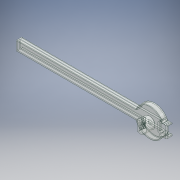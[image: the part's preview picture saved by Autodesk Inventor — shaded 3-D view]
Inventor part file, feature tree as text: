
AUTODESK INVENTOR PART (.ipt)
format: ipt  version: 2018 (Build 220112000, 112)  size: 670,720 bytes
history: native  units: mm
features: sketch x12, extrude x11, projected_geometry x4, fillet x3, mirror x1, shell x1
ambient origin geometry x8: Origin, YZ Plane, XZ Plane, XY Plane, X Axis, Y Axis, Z Axis, Center Point
bodies: 实体1 (feature_tree)
feature tree (32):
  extrude  "拉伸1"  Depth=20.0mm
  extrude  "拉伸2"  Depth=50.0mm
  extrude  "拉伸3"  Depth=17.0mm
  extrude  "拉伸4"  Depth=10.0mm
  extrude  "拉伸5"  Depth=3.0mm TaperAngle=0.0deg
  extrude  "拉伸6"  Depth=20.0mm
  extrude  "拉伸7"  Depth=2.0mm
  sketch  "草图8"  dims[d18=52.0mm d19=4.0mm d20=0.0mm]
  extrude  "拉伸8"  Depth=4.0mm TaperAngle=0.0deg
  extrude  "拉伸9"  Depth=4.0mm TaperAngle=0.0deg
  mirror  "镜像1"
  shell  "抽壳1"  Thickness=6.0mm
  extrude  "拉伸10"  Depth=5.0mm
  extrude  "拉伸11"  Depth=7.0mm TaperAngle=0.0deg
  fillet  "圆角1"  Radius=30.0mm
  fillet  "圆角2"  Radius=26.0mm
  fillet  "圆角3"  Radius=7.0mm
  sketch  "草图1"  dims[d0=20.0mm d1=4.0mm]
  sketch  "草图2"  dims[d2=15.0mm d3=0.0mm d4=50.0mm]
  sketch  "草图3"  dims[d5=17.0mm d6=230.0mm]
  sketch  "草图4"  dims[d7=10.0mm d8=0.0mm d9=245.0mm]
  projected_geometry  "投影回路1"
  sketch  "草图5"  dims[d10=13.0mm d11=3.0mm d12=0.0mm]
  projected_geometry  "投影回路2"
  sketch  "草图6"  dims[d13=20.0mm d14=30.0mm]
  sketch  "草图7"  dims[d15=2.0mm d17=2.0mm]
  projected_geometry  "投影回路5"
  sketch  "草图9"  dims[d21=0.5mm d22=4.0mm d23=2.0mm d24=0.0mm d25=0.0mm d26=6.0mm]
  projected_geometry  "投影回路6"
  sketch  "草图10"  dims[d27=10.75mm d28=0.0mm d30=5.0mm]
  sketch  "草图11"  dims[d31=20.0mm d32=10.75mm d33=0.0mm d34=30.0mm d35=26.0mm d36=7.0mm d37=0.0mm]
  sketch  "草图12"  dims[d38=3.0mm d39=2.5mm d40=2.5mm d41=10.0mm d42=0.0mm d43=1.5mm d44=5.0mm d45=10.0mm d46=0.0mm d47=3.0mm d48=0.5mm d49=5.0mm d50=0.0mm d51=1.0mm d52=1.0mm d53=1.0mm]
